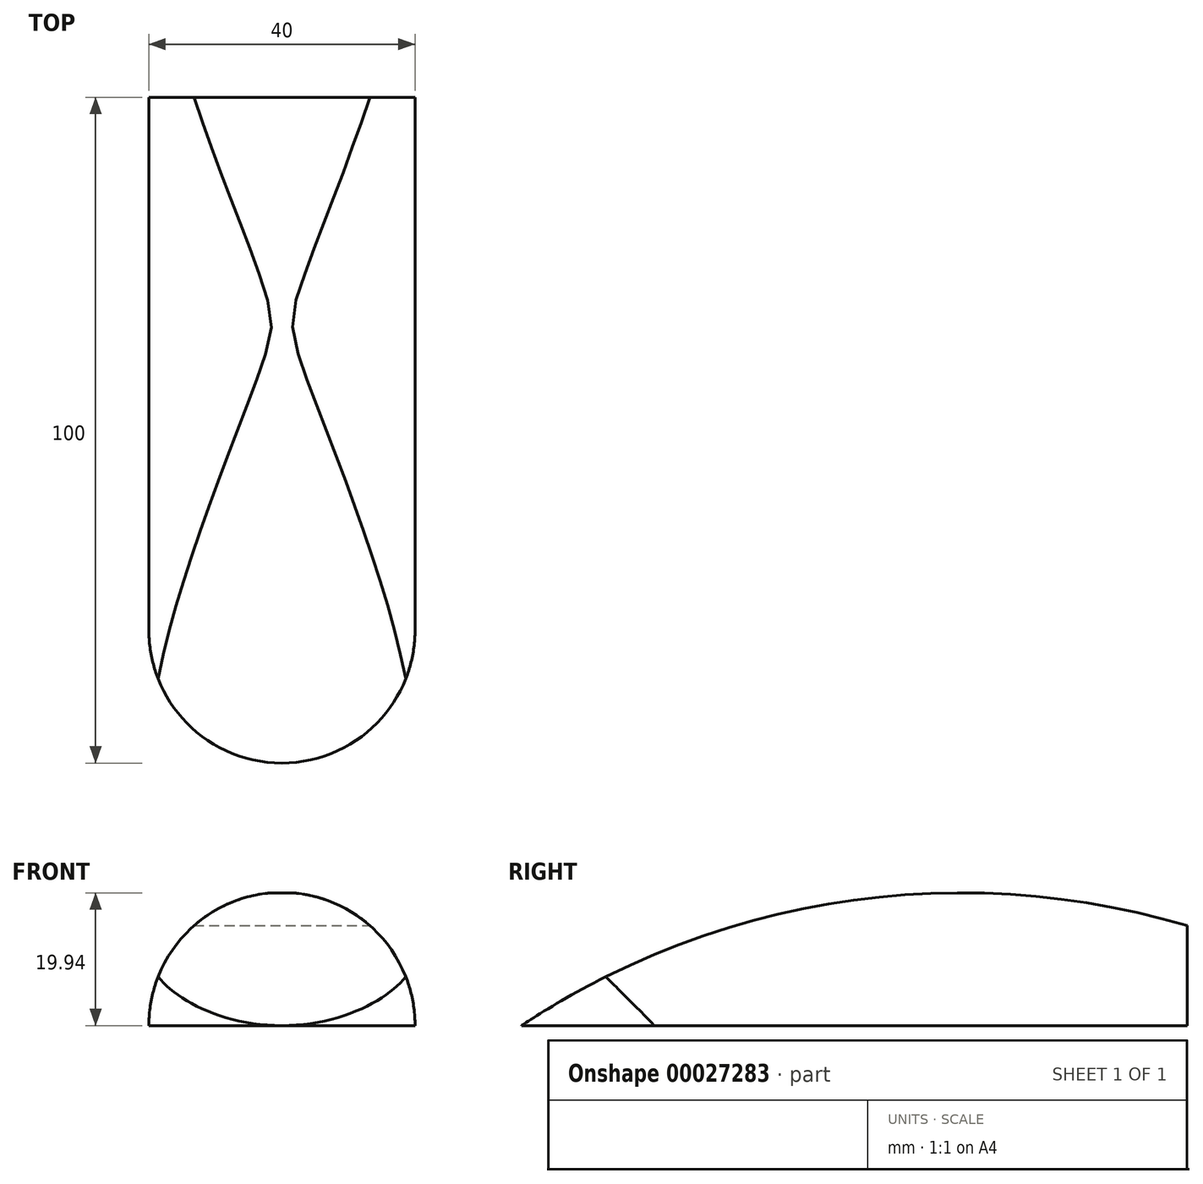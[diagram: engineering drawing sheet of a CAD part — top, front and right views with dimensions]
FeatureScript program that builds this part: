
annotation { "Feature Type Name" : "Feature", "Feature Type Description" : "" }
export const myFeature = defineFeature(function(context is Context, id is Id, definition is map)
    precondition{}
    {
        {
            var Q0;
            Q0=qCreatedBy(makeId("Top.planeOp"),FACE);
            var sketch = newSketch(context, id + "F0", { "sketchPlane" : qUnion([Q0])});
            skPoint(sketch, "E0.rect.middle", {"position": v(0, 0) * mm});
            skLineSegment(sketch, "E1.rect.bottom", {"start": v(-20, 50) * mm, "end": v(20, 50) * mm});
            skLineSegment(sketch, "E1.rect.top", {"start": v(-20, -50) * mm, "end": v(20, -50) * mm});
            skLineSegment(sketch, "E1.rect.left", {"start": v(-20, 50) * mm, "end": v(-20, -50) * mm});
            skLineSegment(sketch, "E1.rect.right", {"start": v(20, 50) * mm, "end": v(20, -50) * mm});
            skSolve(sketch);
        }
        {
            var Q0;
            Q0=qSketchRegion(id+"F0",true);
            extrude(context, id + "F1", {"entities" : qUnion([Q0]), "depth" : 30 * mm});
        }
        {
            var Q0;
            Q0=makeQuery(id+"F1.opExtrude","SWEPT_FACE",FACE,{"disambiguationData":[OSD([sQuery(id+"F0.wireOp",EDGE,"E1.rect.top")])]});
            var sketch = newSketch(context, id + "F2", { "sketchPlane" : qUnion([Q0])});
            skArc(sketch, "E2", {"start": v(20, 15) * mm, "mid": v(0, 30) * mm, "end": v(-20, 15) * mm});
            skLineSegment(sketch, "E3", {"start": v(-20, 15) * mm, "end": v(-20, 30) * mm});
            skLineSegment(sketch, "E4", {"start": v(-20, 30) * mm, "end": v(20, 30) * mm});
            skLineSegment(sketch, "E5", {"start": v(20, 30) * mm, "end": v(20, 15) * mm});
            skSolve(sketch);
        }
        {
            var Q0;
            Q0=qSketchRegion(id+"F2",true);
            extrude(context, id + "F3", {"entities" : qUnion([Q0]), "operationType" : NewBodyOperationType.REMOVE, "endBound" : BoundingType.THROUGH_ALL, "oppositeDirection" : true, "depth" : 25 * mm});
        }
        {
            var Q0;
            Q0=makeQuery(id+"F1.opExtrude","SWEPT_FACE",FACE,{"disambiguationData":[OSD([sQuery(id+"F0.wireOp",EDGE,"E1.rect.right")])]});
            var sketch = newSketch(context, id + "F4", { "sketchPlane" : qUnion([Q0])});
            skArc(sketch, "E6", {"start": v(50, 15) * mm, "mid": v(-1.67, 18.62) * mm, "end": v(-50, 0) * mm});
            skLineSegment(sketch, "E7.0", {"start": v(-50, 15) * mm, "end": v(-50, 30) * mm});
            skLineSegment(sketch, "E8", {"start": v(-50, 30) * mm, "end": v(50, 30) * mm});
            skLineSegment(sketch, "E9.0", {"start": v(-50, 15) * mm, "end": v(-50, 0) * mm});
            skLineSegment(sketch, "E10.0", {"start": v(50, 30) * mm, "end": v(50, 15) * mm});
            skSolve(sketch);
        }
        {
            var Q0;
            Q0=qSketchRegion(id+"F4",true);
            extrude(context, id + "F5", {"entities" : qUnion([Q0]), "operationType" : NewBodyOperationType.REMOVE, "endBound" : BoundingType.THROUGH_ALL, "oppositeDirection" : true, "depth" : 25 * mm});
        }
        {
            var Q0;
            Q0=makeQuery(id+"F1.opExtrude","SWEPT_FACE",FACE,{"disambiguationData":[OSD([sQuery(id+"F0.wireOp",EDGE,"E1.rect.bottom")])]});
            var sketch = newSketch(context, id + "F6", { "sketchPlane" : qUnion([Q0])});
            skArc(sketch, "E11", {"start": v(20, 0) * mm, "mid": v(0, 20) * mm, "end": v(-20, 0) * mm});
            skLineSegment(sketch, "E12.0", {"start": v(-20, 15) * mm, "end": v(-20, 0) * mm});
            skLineSegment(sketch, "E13", {"start": v(-17.83, 19.94) * mm, "end": v(17.83, 19.94) * mm});
            skLineSegment(sketch, "E14.0", {"start": v(20, 15) * mm, "end": v(20, 0) * mm});
            skLineSegment(sketch, "E15", {"start": v(-20, 15) * mm, "end": v(-20, 19.94) * mm});
            skLineSegment(sketch, "E16", {"start": v(-20, 19.94) * mm, "end": v(-17.83, 19.94) * mm});
            skLineSegment(sketch, "E17", {"start": v(20, 15) * mm, "end": v(20, 19.94) * mm});
            skLineSegment(sketch, "E18", {"start": v(20, 19.94) * mm, "end": v(17.83, 19.94) * mm});
            skSolve(sketch);
        }
        {
            var Q0;
            Q0=qSketchRegion(id+"F6",true);
            extrude(context, id + "F7", {"entities" : qUnion([Q0]), "operationType" : NewBodyOperationType.REMOVE, "endBound" : BoundingType.THROUGH_ALL, "oppositeDirection" : true, "depth" : 25 * mm});
        }
        {
            var Q0;
            Q0=makeQuery(id+"F1.opExtrude","CAP_FACE",FACE,{"disambiguationData":[OSD([sQuery(id+"F0.wireOp",EDGE,"E1.rect.bottom"),sQuery(id+"F0.wireOp",EDGE,"E1.rect.top"),sQuery(id+"F0.wireOp",EDGE,"E1.rect.left"),sQuery(id+"F0.wireOp",EDGE,"E1.rect.right")])],"isStart":true});
            var sketch = newSketch(context, id + "F8", { "sketchPlane" : qUnion([Q0])});
            skLineSegment(sketch, "E19.0", {"start": v(-20, 50) * mm, "end": v(20, 50) * mm});
            skLineSegment(sketch, "E20.0", {"start": v(-20, -50) * mm, "end": v(-20, 50) * mm});
            skLineSegment(sketch, "E21.0", {"start": v(20, -50) * mm, "end": v(20, 50) * mm});
            skArc(sketch, "E22", {"start": v(20, 30.12) * mm, "mid": v(0, 50) * mm, "end": v(-20, 30.12) * mm});
            skSolve(sketch);
        }
        {
            var Q0;
            {var subQ1=sQuery(id+"F8.wireOp",EDGE,"E19.0");var subQ3=sQuery(id+"F8.wireOp",EDGE,"E20.0");var subQ5=makeQuery(id+"F8.imprint","INTERSECT",VERTEX,{"derivedFrom":[subQ1,subQ3]});Q0=makeQuery(id+"F8.imprint","IMPRINT",FACE,{"disambiguationData":[TD([[makeQuery(id+"F8.imprint","IMPRINT",EDGE,{"disambiguationData":[TD([[subQ5,-1.0]])],"derivedFrom":subQ1}),-1.0]])]});}
            var Q1;
            {var subQ1=sQuery(id+"F8.wireOp",EDGE,"E19.0");var subQ3=sQuery(id+"F8.wireOp",EDGE,"E21.0");var subQ5=makeQuery(id+"F8.imprint","INTERSECT",VERTEX,{"derivedFrom":[subQ1,subQ3]});Q1=makeQuery(id+"F8.imprint","IMPRINT",FACE,{"disambiguationData":[TD([[makeQuery(id+"F8.imprint","IMPRINT",EDGE,{"disambiguationData":[TD([[subQ5,1.0]])],"derivedFrom":subQ1}),-1.0]])]});}
            extrude(context, id + "F9", {"entities" : qUnion([Q0, Q1]), "operationType" : NewBodyOperationType.REMOVE, "oppositeDirection" : true, "depth" : 25 * mm});
        }
        {
            var Q0;
            Q0=qCreatedBy(makeId("Right.planeOp"),FACE);
            cPlane(context, id + "F10", {"entities" : qUnion([Q0]), "cplaneType" : CPlaneType.OFFSET, "offset" : 20 * mm, "width" : 150 * mm, "height" : 150 * mm});
        }
    });
